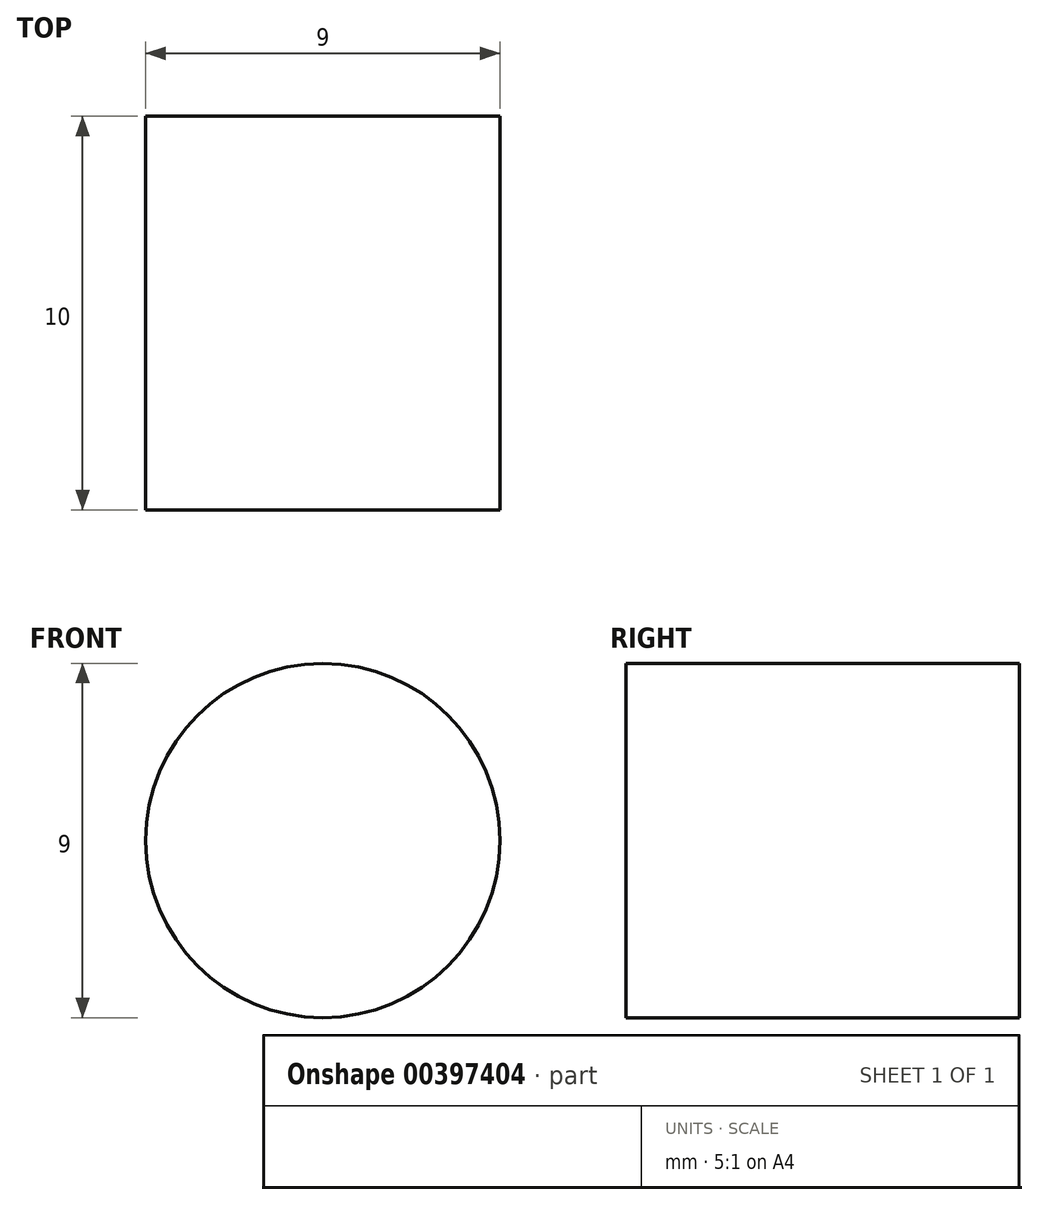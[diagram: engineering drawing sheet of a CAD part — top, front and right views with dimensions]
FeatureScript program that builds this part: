
annotation { "Feature Type Name" : "Feature", "Feature Type Description" : "" }
export const myFeature = defineFeature(function(context is Context, id is Id, definition is map)
    precondition{}
    {
        {
            var Q0;
            Q0=qCreatedBy(makeId("Front.planeOp"),FACE);
            var sketch = newSketch(context, id + "F0", { "sketchPlane" : qUnion([Q0])});
            skCircle(sketch, "E0", {"center": v(0, 0) * mm, "radius": 4.5 * mm});
            skSolve(sketch);
        }
        {
            var Q0;
            Q0=makeQuery(id+"F0.imprint","IMPRINT",FACE,{"disambiguationData":[TD([[makeQuery(id+"F0.imprint","IMPRINT",EDGE,{"derivedFrom":sQuery(id+"F0.wireOp",EDGE,"E0")}),1.0]])]});
            extrude(context, id + "F1", {"entities" : qUnion([Q0]), "oppositeDirection" : true, "depth" : 10 * mm});
        }
    });
